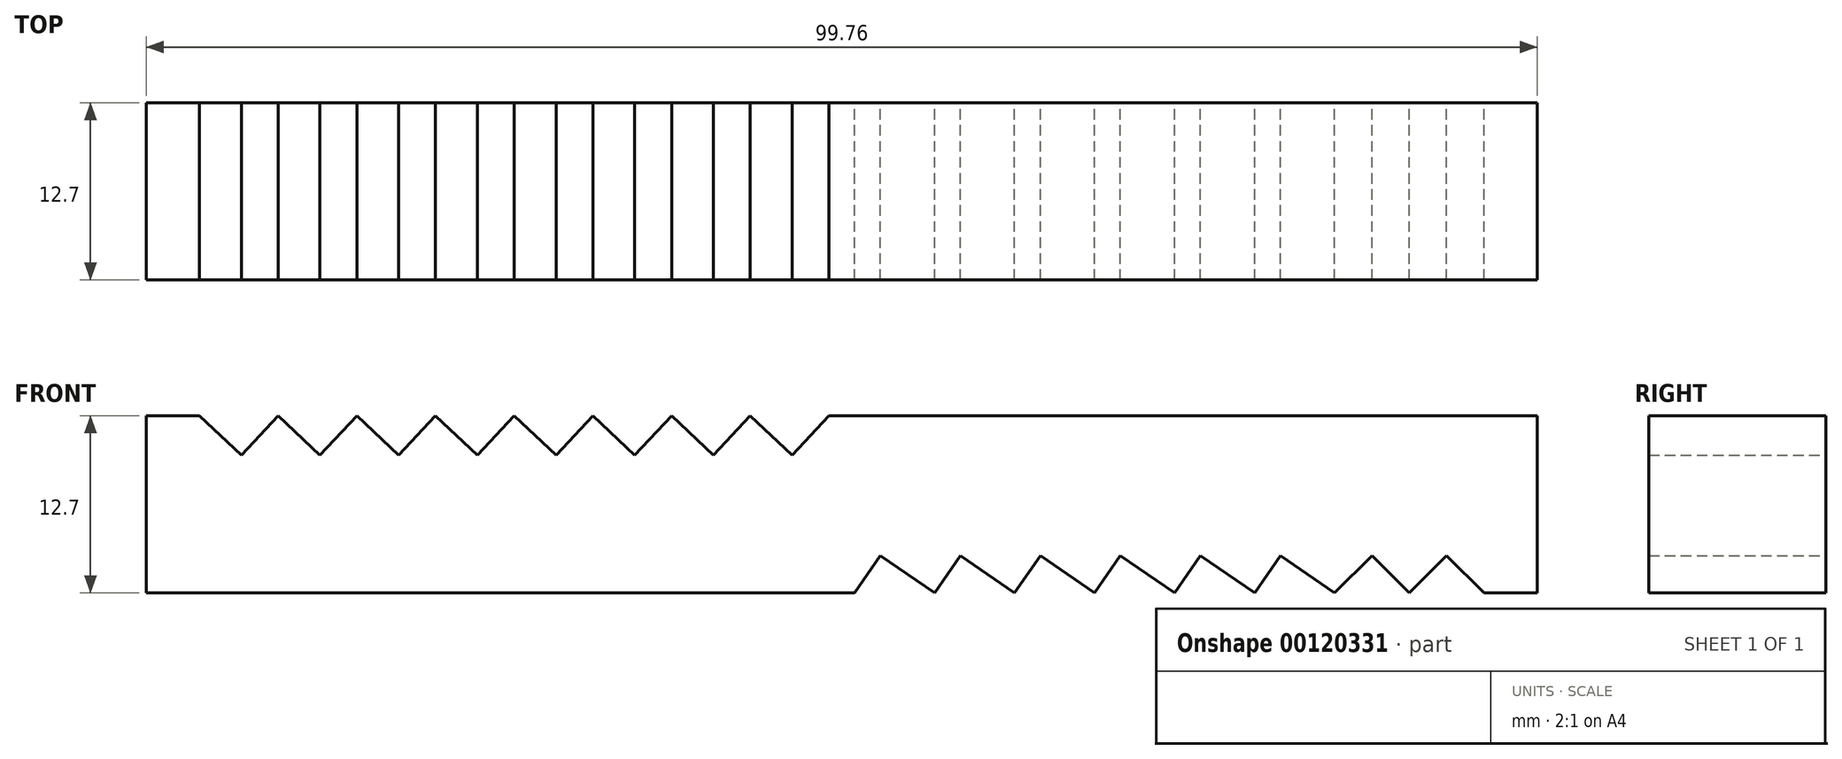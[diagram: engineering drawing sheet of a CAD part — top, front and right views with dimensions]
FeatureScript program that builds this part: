
annotation { "Feature Type Name" : "Feature", "Feature Type Description" : "" }
export const myFeature = defineFeature(function(context is Context, id is Id, definition is map)
    precondition{}
    {
        {
            var Q0;
            Q0=qCreatedBy(makeId("Front.planeOp"),FACE);
            var sketch = newSketch(context, id + "F0", { "sketchPlane" : qUnion([Q0])});
            skLineSegment(sketch, "E0", {"start": v(0, 3.06) * mm, "end": v(-2.64, 0.25) * mm});
            skLineSegment(sketch, "E1", {"start": v(-2.64, 0.25) * mm, "end": v(-5.64, 3.06) * mm});
            skLineSegment(sketch, "E2", {"start": v(-5.64, 3.06) * mm, "end": v(-8.28, 0.25) * mm});
            skLineSegment(sketch, "E3", {"start": v(-8.28, 0.25) * mm, "end": v(-11.29, 3.06) * mm});
            skLineSegment(sketch, "E4", {"start": v(-11.29, 3.06) * mm, "end": v(-13.92, 0.25) * mm});
            skLineSegment(sketch, "E5", {"start": v(-13.92, 0.25) * mm, "end": v(-16.93, 3.06) * mm});
            skLineSegment(sketch, "E6", {"start": v(-16.93, 3.06) * mm, "end": v(-19.57, 0.25) * mm});
            skLineSegment(sketch, "E7", {"start": v(-19.57, 0.25) * mm, "end": v(-22.57, 3.06) * mm});
            skLineSegment(sketch, "E8", {"start": v(-22.57, 3.06) * mm, "end": v(-25.21, 0.25) * mm});
            skLineSegment(sketch, "E9", {"start": v(-25.21, 0.25) * mm, "end": v(-28.22, 3.06) * mm});
            skLineSegment(sketch, "E10", {"start": v(-48.96, 3.06) * mm, "end": v(-48.96, -9.64) * mm});
            skLineSegment(sketch, "E11", {"start": v(-48.96, -9.64) * mm, "end": v(0, -9.64) * mm});
            skLineSegment(sketch, "E12", {"start": v(0, 3.06) * mm, "end": v(50.8, 3.06) * mm});
            skLineSegment(sketch, "E13", {"start": v(50.8, 3.06) * mm, "end": v(50.8, -9.64) * mm});
            skPoint(sketch, "E13.endSnap0", {"position": v(-24.48, -9.64) * mm});
            skLineSegment(sketch, "E14", {"start": v(50.8, -9.64) * mm, "end": v(47, -9.64) * mm});
            skLineSegment(sketch, "E15", {"start": v(47, -9.64) * mm, "end": v(44.3, -6.96) * mm});
            skLineSegment(sketch, "E16", {"start": v(44.3, -6.96) * mm, "end": v(41.63, -9.64) * mm});
            skLineSegment(sketch, "E17", {"start": v(41.63, -9.64) * mm, "end": v(38.94, -6.96) * mm});
            skLineSegment(sketch, "E18", {"start": v(38.94, -6.96) * mm, "end": v(36.27, -9.64) * mm});
            skLineSegment(sketch, "E19", {"start": v(36.27, -9.64) * mm, "end": v(32.38, -6.96) * mm});
            skLineSegment(sketch, "E20", {"start": v(32.38, -6.96) * mm, "end": v(30.53, -9.64) * mm});
            skLineSegment(sketch, "E21", {"start": v(30.53, -9.64) * mm, "end": v(26.64, -6.96) * mm});
            skLineSegment(sketch, "E22", {"start": v(26.64, -6.96) * mm, "end": v(24.8, -9.64) * mm});
            skLineSegment(sketch, "E23", {"start": v(24.8, -9.64) * mm, "end": v(20.9, -6.96) * mm});
            skLineSegment(sketch, "E24", {"start": v(20.9, -6.96) * mm, "end": v(19.05, -9.64) * mm});
            skLineSegment(sketch, "E25", {"start": v(19.05, -9.64) * mm, "end": v(15.16, -6.96) * mm});
            skLineSegment(sketch, "E26", {"start": v(15.16, -6.96) * mm, "end": v(13.32, -9.64) * mm});
            skLineSegment(sketch, "E27", {"start": v(13.32, -9.64) * mm, "end": v(9.43, -6.96) * mm});
            skLineSegment(sketch, "E28", {"start": v(9.43, -6.96) * mm, "end": v(7.58, -9.64) * mm});
            skLineSegment(sketch, "E29", {"start": v(7.58, -9.64) * mm, "end": v(3.69, -6.96) * mm});
            skLineSegment(sketch, "E30", {"start": v(3.69, -6.96) * mm, "end": v(1.84, -9.64) * mm});
            skLineSegment(sketch, "E31", {"start": v(1.84, -9.64) * mm, "end": v(0, -9.64) * mm});
            skLineSegment(sketch, "E32", {"start": v(-28.22, 3.06) * mm, "end": v(-30.86, 0.25) * mm});
            skLineSegment(sketch, "E33", {"start": v(-30.86, 0.25) * mm, "end": v(-33.86, 3.06) * mm});
            skLineSegment(sketch, "E34", {"start": v(-33.86, 3.06) * mm, "end": v(-36.5, 0.25) * mm});
            skLineSegment(sketch, "E35", {"start": v(-36.5, 0.25) * mm, "end": v(-39.5, 3.06) * mm});
            skLineSegment(sketch, "E36", {"start": v(-39.5, 3.06) * mm, "end": v(-42.14, 0.25) * mm});
            skLineSegment(sketch, "E37", {"start": v(-42.14, 0.25) * mm, "end": v(-45.15, 3.06) * mm});
            skLineSegment(sketch, "E38", {"start": v(-45.15, 3.06) * mm, "end": v(-48.96, 3.06) * mm});
            skSolve(sketch);
        }
        {
            var Q0;
            Q0 = qSketchRegion(id + "F0", true);
            extrude(context, id + "F1", {"entities" : qUnion([Q0]), "depth" : 12.7 * mm});
        }
    });
